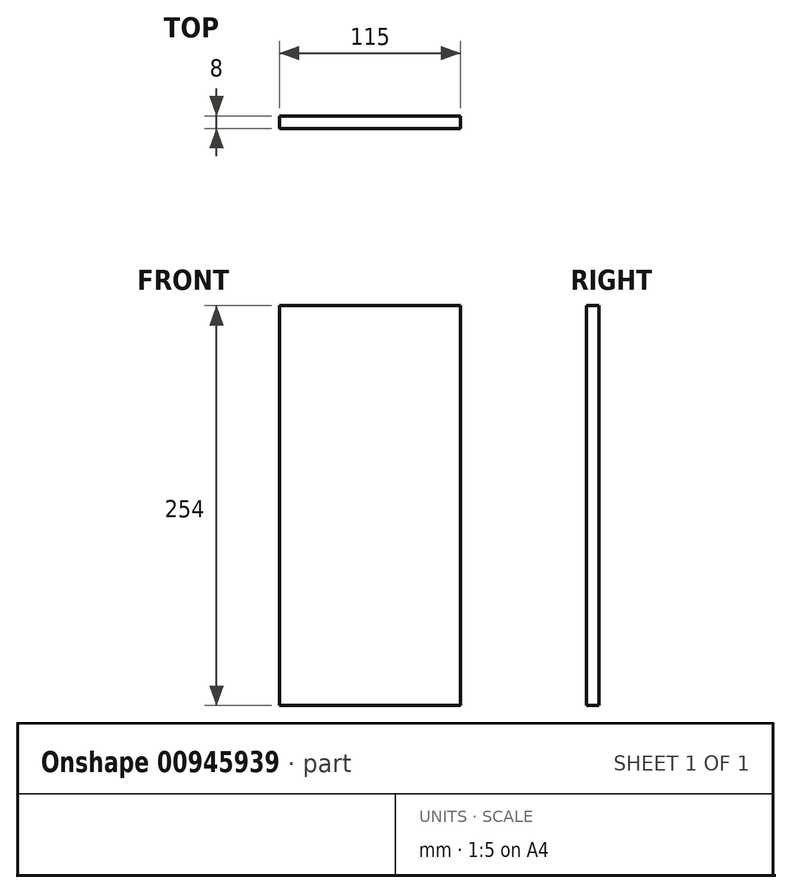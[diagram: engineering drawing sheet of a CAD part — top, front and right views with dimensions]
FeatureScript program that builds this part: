
annotation { "Feature Type Name" : "Feature", "Feature Type Description" : "" }
export const myFeature = defineFeature(function(context is Context, id is Id, definition is map)
    precondition{}
    {
        {
            var Q0;
            Q0=qCreatedBy(makeId("Front.planeOp"),FACE);
            var sketch = newSketch(context, id + "F0", { "sketchPlane" : qUnion([Q0])});
            skLineSegment(sketch, "E0.bottom", {"start": v(0, 0) * mm, "end": v(115, 0) * mm});
            skLineSegment(sketch, "E0.top", {"start": v(0, 254) * mm, "end": v(115, 254) * mm});
            skLineSegment(sketch, "E0.left", {"start": v(0, 0) * mm, "end": v(0, 254) * mm});
            skLineSegment(sketch, "E0.right", {"start": v(115, 0) * mm, "end": v(115, 254) * mm});
            skSolve(sketch);
        }
        {
            var Q0;
            Q0 = qSketchRegion(id + "F0", true);
            extrude(context, id + "F1", {"entities" : qUnion([Q0]), "depth" : 8 * mm, "offsetDistance" : 25 * mm});
        }
    });
